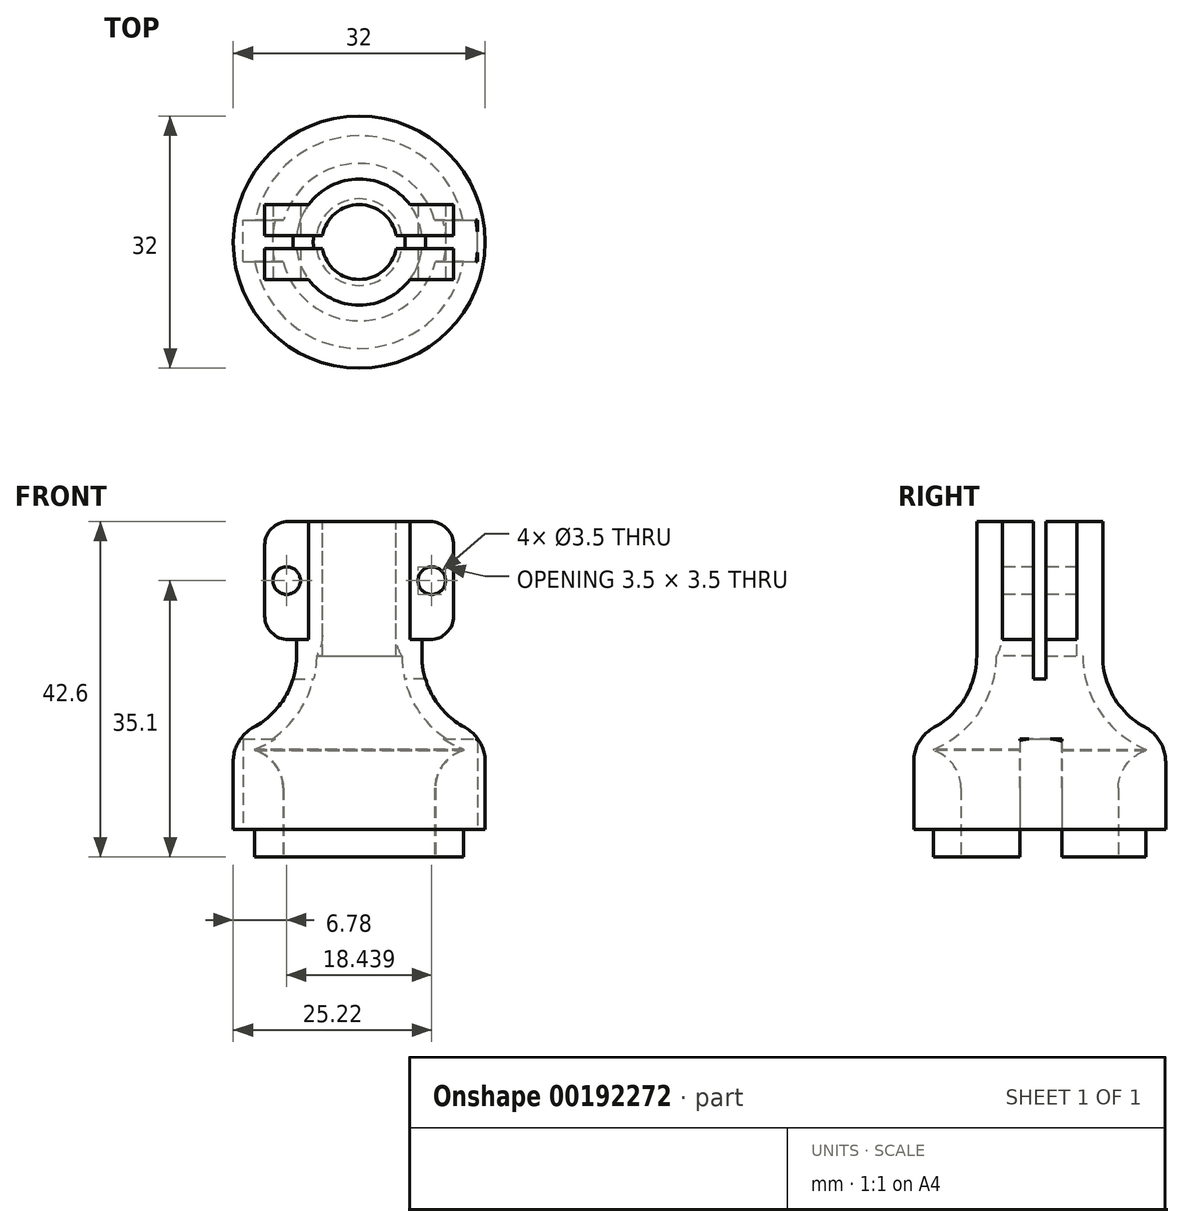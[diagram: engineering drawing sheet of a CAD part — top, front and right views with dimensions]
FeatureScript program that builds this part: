
annotation { "Feature Type Name" : "Feature", "Feature Type Description" : "" }
export const myFeature = defineFeature(function(context is Context, id is Id, definition is map)
    precondition{}
    {
        {
            var Q0;
            Q0=qCreatedBy(makeId("Front.planeOp"),FACE);
            var sketch = newSketch(context, id + "F0", { "sketchPlane" : qUnion([Q0])});
            skLineSegment(sketch, "E0", {"start": v(0, 0) * mm, "end": v(16, 0) * mm});
            skLineSegment(sketch, "E1", {"start": v(16, 0) * mm, "end": v(16, 12) * mm});
            skPoint(sketch, "E2.endSnap0", {"position": v(8, 12) * mm});
            skLineSegment(sketch, "E3", {"start": v(8, 22) * mm, "end": v(8, 34.1) * mm});
            skLineSegment(sketch, "E4", {"start": v(8, 34.1) * mm, "end": v(0, 34.1) * mm});
            skArc(sketch, "E5", {"start": v(8, 22) * mm, "mid": v(10.25, 15.6) * mm, "end": v(16, 12) * mm});
            skLineSegment(sketch, "E6.1", {"start": v(0, 2.5) * mm, "end": v(13.5, 2.5) * mm});
            skLineSegment(sketch, "E6.2", {"start": v(13.5, 2.5) * mm, "end": v(13.5, 10.17) * mm});
            skArc(sketch, "E6.3", {"start": v(5.5, 22) * mm, "mid": v(7.69, 14.86) * mm, "end": v(13.5, 10.17) * mm});
            skLineSegment(sketch, "E7", {"start": v(0, 31.6) * mm, "end": v(0, 34.1) * mm});
            skLineSegment(sketch, "E8", {"start": v(0, 0) * mm, "end": v(0, 2.5) * mm});
            skLineSegment(sketch, "E9", {"start": v(0, 31.6) * mm, "end": v(0, 22) * mm});
            skLineSegment(sketch, "E10", {"start": v(0, 22) * mm, "end": v(5.5, 22) * mm});
            skSolve(sketch);
        }
        {
            var Q0;
            Q0 = qSketchRegion(id + "F0", true);
            var Q1;
            Q1=sQuery(id+"F0.wireOp",EDGE,"E8");
            revolve(context, id + "F1", {"entities" : qUnion([Q0]), "axis" : qUnion([Q1]), "revolveType" : RevolveType.FULL});
        }
        {
            var Q0;
            Q0=makeQuery(id+"F1.opRevolve","SWEPT_EDGE",EDGE,{"disambiguationData":[OSD([sQuery(id+"F0.wireOp",EDGE,"E1"),sQuery(id+"F0.wireOp",EDGE,"E5")])]});
            fillet(context, id + "F2", {"entities" : qUnion([Q0]), "radius" : 5 * mm, "tangentPropagation" : true, "allowEdgeOverflow" : false});
        }
        {
            var Q0;
            Q0=makeQuery(id+"F1.opRevolve","SWEPT_FACE",FACE,{"disambiguationData":[OSD([sQuery(id+"F0.wireOp",EDGE,"E0")])]});
            var sketch = newSketch(context, id + "F3", { "sketchPlane" : qUnion([Q0])});
            skCircle(sketch, "E11", {"center": v(0, 0) * mm, "radius": 13.5 * mm});
            skSolve(sketch);
        }
        {
            var Q0;
            Q0=makeQuery(id+"F3.imprint","IMPRINT",FACE,{"disambiguationData":[TD([[makeQuery(id+"F3.imprint","IMPRINT",EDGE,{"derivedFrom":sQuery(id+"F3.wireOp",EDGE,"E11")}),1.0]])]});
            extrude(context, id + "F4", {"entities" : qUnion([Q0]), "operationType" : NewBodyOperationType.REMOVE, "oppositeDirection" : true, "depth" : 8 * mm});
        }
        {
            var Q0;
            Q0=makeQuery(id+"F1.opRevolve","SWEPT_FACE",FACE,{"disambiguationData":[OSD([sQuery(id+"F0.wireOp",EDGE,"E4")])]});
            var sketch = newSketch(context, id + "F5", { "sketchPlane" : qUnion([Q0])});
            skCircle(sketch, "E12", {"center": v(0, 0) * mm, "radius": 4.75 * mm});
            skSolve(sketch);
        }
        {
            var Q0;
            Q0 = qSketchRegion(id + "F5", true);
            extrude(context, id + "F6", {"entities" : qUnion([Q0]), "operationType" : NewBodyOperationType.REMOVE, "oppositeDirection" : true, "depth" : 25 * mm});
        }
        {
            var Q0;
            Q0=makeQuery(id+"F1.opRevolve","SWEPT_FACE",FACE,{"disambiguationData":[OSD([sQuery(id+"F0.wireOp",EDGE,"E4")])]});
            var sketch = newSketch(context, id + "F7", { "sketchPlane" : qUnion([Q0])});
            skCircle(sketch, "E13", {"center": v(0, 0) * mm, "radius": 8 * mm});
            skLineSegment(sketch, "E14", {"start": v(0, 0) * mm, "end": v(0, 4.75) * mm});
            skLineSegment(sketch, "E15", {"start": v(0, 4.75) * mm, "end": v(12, 4.75) * mm});
            skLineSegment(sketch, "E16", {"start": v(0, -4.75) * mm, "end": v(12, -4.75) * mm});
            skLineSegment(sketch, "E17", {"start": v(12, -4.75) * mm, "end": v(12, 4.75) * mm});
            skLineSegment(sketch, "E18", {"start": v(0, 4.75) * mm, "end": v(-12, 4.75) * mm});
            skLineSegment(sketch, "E19", {"start": v(0, -4.75) * mm, "end": v(-12, -4.75) * mm});
            skLineSegment(sketch, "E20", {"start": v(-12, -4.75) * mm, "end": v(-12, 4.75) * mm});
            skCircle(sketch, "E21", {"center": v(0, 0) * mm, "radius": 4.75 * mm});
            skSolve(sketch);
        }
        {
            var Q0;
            Q0 = qSketchRegion(id + "F7", true);
            extrude(context, id + "F8", {"entities" : qUnion([Q0]), "operationType" : NewBodyOperationType.ADD, "oppositeDirection" : true, "depth" : 10 * mm});
        }
        {
            var Q0;
            Q0 = qSketchRegion(id + "F7", true);
            extrude(context, id + "F9", {"entities" : qUnion([Q0]), "operationType" : NewBodyOperationType.ADD, "depth" : 5 * mm});
        }
        {
            var Q0;
            {var subQ0=sQuery(id+"F7.wireOp",EDGE,"E19");Q0=makeQuery(id+"F9.boolean.opBoolean","MERGE",FACE,{"derivedFrom":[makeQuery(id+"F8.opExtrude","SWEPT_FACE",FACE,{"disambiguationData":[OSD([subQ0])]}),makeQuery(id+"F9.opExtrude","SWEPT_FACE",FACE,{"disambiguationData":[OSD([subQ0])]})]});}
            var sketch = newSketch(context, id + "F10", { "sketchPlane" : qUnion([Q0])});
            skLineSegment(sketch, "E22", {"start": v(-12, 31.6) * mm, "end": v(-9.22, 31.6) * mm});
            skPoint(sketch, "E22.endSnap0", {"position": v(-9.22, 39.1) * mm});
            skCircle(sketch, "E23", {"center": v(-9.22, 31.6) * mm, "radius": 1.75 * mm});
            skSolve(sketch);
        }
        {
            var Q0;
            Q0 = qSketchRegion(id + "F10", true);
            extrude(context, id + "F11", {"entities" : qUnion([Q0]), "operationType" : NewBodyOperationType.REMOVE, "oppositeDirection" : true, "depth" : 15 * mm});
        }
        {
            var Q0;
            {var subQ0=sQuery(id+"F7.wireOp",EDGE,"E16");Q0=makeQuery(id+"F9.boolean.opBoolean","MERGE",FACE,{"derivedFrom":[makeQuery(id+"F8.opExtrude","SWEPT_FACE",FACE,{"disambiguationData":[OSD([subQ0])]}),makeQuery(id+"F9.opExtrude","SWEPT_FACE",FACE,{"disambiguationData":[OSD([subQ0])]})]});}
            var sketch = newSketch(context, id + "F12", { "sketchPlane" : qUnion([Q0])});
            skLineSegment(sketch, "E24", {"start": v(12, 31.6) * mm, "end": v(9.22, 31.6) * mm});
            skPoint(sketch, "E24.endSnap0", {"position": v(9.22, 39.1) * mm});
            skCircle(sketch, "E25", {"center": v(9.22, 31.6) * mm, "radius": 1.75 * mm});
            skSolve(sketch);
        }
        {
            var Q0;
            Q0 = qSketchRegion(id + "F12", true);
            extrude(context, id + "F13", {"entities" : qUnion([Q0]), "operationType" : NewBodyOperationType.REMOVE, "oppositeDirection" : true, "depth" : 15 * mm});
        }
        {
            var Q0;
            Q0=makeQuery(id+"F9.opExtrude","CAP_FACE",FACE,{"disambiguationData":[OSD([sQuery(id+"F7.wireOp",EDGE,"E13"),sQuery(id+"F7.wireOp",EDGE,"E15"),sQuery(id+"F7.wireOp",EDGE,"E16"),sQuery(id+"F7.wireOp",EDGE,"E17"),sQuery(id+"F7.wireOp",EDGE,"E18"),sQuery(id+"F7.wireOp",EDGE,"E19"),sQuery(id+"F7.wireOp",EDGE,"E20"),sQuery(id+"F7.wireOp",EDGE,"E21")])],"isStart":false});
            var sketch = newSketch(context, id + "F14", { "sketchPlane" : qUnion([Q0])});
            skLineSegment(sketch, "E26", {"start": v(-12, 0) * mm, "end": v(-12, 0.8) * mm});
            skLineSegment(sketch, "E27", {"start": v(-12, 0.8) * mm, "end": v(-4.68, 0.8) * mm});
            skLineSegment(sketch, "E28", {"start": v(-12, 0) * mm, "end": v(-12, -0.8) * mm});
            skLineSegment(sketch, "E29", {"start": v(-12, -0.8) * mm, "end": v(-4.68, -0.8) * mm});
            skLineSegment(sketch, "E30", {"start": v(12, 0) * mm, "end": v(12, 0.8) * mm});
            skLineSegment(sketch, "E31", {"start": v(12, 0.8) * mm, "end": v(4.68, 0.8) * mm});
            skLineSegment(sketch, "E32", {"start": v(12, 0) * mm, "end": v(12, -0.8) * mm});
            skLineSegment(sketch, "E33", {"start": v(12, -0.8) * mm, "end": v(4.68, -0.8) * mm});
            skSolve(sketch);
        }
        {
            var Q0;
            Q0 = qSketchRegion(id + "F14", true);
            var Q1;
            Q1=makeQuery(id+"F14.imprint","IMPRINT",FACE,{"disambiguationData":[TD([[makeQuery(id+"F14.imprint","IMPRINT",EDGE,{"derivedFrom":sQuery(id+"F14.wireOp",EDGE,"E26")}),-1.0]])]});
            var Q2;
            Q2=makeQuery(id+"F14.imprint","IMPRINT",FACE,{"disambiguationData":[TD([[makeQuery(id+"F14.imprint","IMPRINT",EDGE,{"derivedFrom":sQuery(id+"F14.wireOp",EDGE,"E30")}),1.0]])]});
            extrude(context, id + "F15", {"entities" : qUnion([Q0, Q1, Q2]), "operationType" : NewBodyOperationType.REMOVE, "oppositeDirection" : true, "depth" : 20 * mm});
        }
        {
            var Q0;
            {var subQ0=sQuery(id+"F7.wireOp",EDGE,"E19");var subQ1=sQuery(id+"F7.wireOp",EDGE,"E20");Q0=makeQuery(id+"F15.boolean.opBoolean","SPLIT",EDGE,{"disambiguationData":[TD([makeQuery(id+"F8.opExtrude","SWEPT_FACE",FACE,{"disambiguationData":[OSD([subQ0])]})])],"derivedFrom":makeQuery(id+"F9.opExtrude","CAP_EDGE",EDGE,{"disambiguationData":[OSD([subQ1])],"isStart":false})});}
            var Q1;
            {var subQ0=sQuery(id+"F7.wireOp",EDGE,"E17");var subQ1=sQuery(id+"F7.wireOp",EDGE,"E16");Q1=makeQuery(id+"F15.boolean.opBoolean","SPLIT",EDGE,{"disambiguationData":[TD([makeQuery(id+"F8.opExtrude","SWEPT_FACE",FACE,{"disambiguationData":[OSD([subQ1])]})])],"derivedFrom":makeQuery(id+"F9.opExtrude","CAP_EDGE",EDGE,{"disambiguationData":[OSD([subQ0])],"isStart":false})});}
            var Q2;
            {var subQ0=sQuery(id+"F7.wireOp",EDGE,"E18");var subQ1=sQuery(id+"F7.wireOp",EDGE,"E20");Q2=makeQuery(id+"F15.boolean.opBoolean","SPLIT",EDGE,{"disambiguationData":[TD([makeQuery(id+"F8.opExtrude","SWEPT_FACE",FACE,{"disambiguationData":[OSD([subQ0])]})])],"derivedFrom":makeQuery(id+"F9.opExtrude","CAP_EDGE",EDGE,{"disambiguationData":[OSD([subQ1])],"isStart":false})});}
            var Q3;
            {var subQ0=sQuery(id+"F7.wireOp",EDGE,"E15");var subQ1=sQuery(id+"F7.wireOp",EDGE,"E17");Q3=makeQuery(id+"F15.boolean.opBoolean","SPLIT",EDGE,{"disambiguationData":[TD([makeQuery(id+"F8.opExtrude","SWEPT_FACE",FACE,{"disambiguationData":[OSD([subQ0])]})])],"derivedFrom":makeQuery(id+"F9.opExtrude","CAP_EDGE",EDGE,{"disambiguationData":[OSD([subQ1])],"isStart":false})});}
            var Q4;
            {var subQ0=sQuery(id+"F7.wireOp",EDGE,"E19");var subQ1=sQuery(id+"F7.wireOp",EDGE,"E20");Q4=makeQuery(id+"F15.boolean.opBoolean","SPLIT",EDGE,{"disambiguationData":[TD([makeQuery(id+"F8.opExtrude","SWEPT_FACE",FACE,{"disambiguationData":[OSD([subQ0])]})])],"derivedFrom":makeQuery(id+"F8.opExtrude","CAP_EDGE",EDGE,{"disambiguationData":[OSD([subQ1])],"isStart":false})});}
            var Q5;
            {var subQ0=sQuery(id+"F7.wireOp",EDGE,"E18");var subQ1=sQuery(id+"F7.wireOp",EDGE,"E20");Q5=makeQuery(id+"F15.boolean.opBoolean","SPLIT",EDGE,{"disambiguationData":[TD([makeQuery(id+"F8.opExtrude","SWEPT_FACE",FACE,{"disambiguationData":[OSD([subQ0])]})])],"derivedFrom":makeQuery(id+"F8.opExtrude","CAP_EDGE",EDGE,{"disambiguationData":[OSD([subQ1])],"isStart":false})});}
            var Q6;
            {var subQ0=sQuery(id+"F7.wireOp",EDGE,"E16");var subQ1=sQuery(id+"F7.wireOp",EDGE,"E17");Q6=makeQuery(id+"F15.boolean.opBoolean","SPLIT",EDGE,{"disambiguationData":[TD([makeQuery(id+"F8.opExtrude","SWEPT_FACE",FACE,{"disambiguationData":[OSD([subQ0])]})])],"derivedFrom":makeQuery(id+"F8.opExtrude","CAP_EDGE",EDGE,{"disambiguationData":[OSD([subQ1])],"isStart":false})});}
            var Q7;
            {var subQ0=sQuery(id+"F7.wireOp",EDGE,"E15");var subQ1=sQuery(id+"F7.wireOp",EDGE,"E17");Q7=makeQuery(id+"F15.boolean.opBoolean","SPLIT",EDGE,{"disambiguationData":[TD([makeQuery(id+"F8.opExtrude","SWEPT_FACE",FACE,{"disambiguationData":[OSD([subQ0])]})])],"derivedFrom":makeQuery(id+"F8.opExtrude","CAP_EDGE",EDGE,{"disambiguationData":[OSD([subQ1])],"isStart":false})});}
            fillet(context, id + "F16", {"entities" : qUnion([Q0, Q1, Q2, Q3, Q4, Q5, Q6, Q7]), "radius" : 3 * mm, "tangentPropagation" : true, "allowEdgeOverflow" : false});
        }
        {
            var Q0;
            Q0=makeQuery(id+"F1.opRevolve","SWEPT_FACE",FACE,{"disambiguationData":[OSD([sQuery(id+"F0.wireOp",EDGE,"E0")])]});
            var sketch = newSketch(context, id + "F17", { "sketchPlane" : qUnion([Q0])});
            skCircle(sketch, "E34", {"center": v(0, 0) * mm, "radius": 13.5 * mm});
            skCircle(sketch, "E35", {"center": v(0, 0) * mm, "radius": 10 * mm});
            skSolve(sketch);
        }
        {
            var Q0;
            Q0=makeQuery(id+"F17.imprint","IMPRINT",FACE,{"disambiguationData":[TD([[makeQuery(id+"F17.imprint","IMPRINT",EDGE,{"derivedFrom":sQuery(id+"F17.wireOp",EDGE,"E34")}),1.0]])]});
            extrude(context, id + "F18", {"entities" : qUnion([Q0]), "oppositeDirection" : true, "depth" : 10 * mm});
        }
        {
            var Q0;
            Q0=makeQuery(id+"F18.opExtrude","CAP_FACE",FACE,{"disambiguationData":[OSD([sQuery(id+"F17.wireOp",EDGE,"E34"),sQuery(id+"F17.wireOp",EDGE,"E35")])],"isStart":true});
            extrude(context, id + "F19", {"entities" : qUnion([Q0]), "operationType" : NewBodyOperationType.ADD, "depth" : 3.5 * mm});
        }
        {
            var Q0;
            Q0=makeQuery(id+"F18.opExtrude","CAP_EDGE",EDGE,{"disambiguationData":[OSD([sQuery(id+"F17.wireOp",EDGE,"E35")])],"isStart":false});
            fillet(context, id + "F20", {"entities" : qUnion([Q0]), "radius" : 5 * mm, "tangentPropagation" : true, "allowEdgeOverflow" : false});
        }
        {
            var Q0;
            {var subQ0=makeQuery(id+"F6.opExtrude","SWEPT_FACE",FACE,{"disambiguationData":[OSD([sQuery(id+"F5.wireOp",EDGE,"E12")])]});var subQ1=makeQuery(id+"F1.opRevolve","SWEPT_FACE",FACE,{"disambiguationData":[OSD([sQuery(id+"F0.wireOp",EDGE,"E10")])]});Q0=makeQuery(id+"F15.boolean.opBoolean","SPLIT",EDGE,{"disambiguationData":[TD([makeQuery(id+"F15.opExtrude","SWEPT_FACE",FACE,{"disambiguationData":[OSD([sQuery(id+"F14.wireOp",EDGE,"E29")])]})])],"derivedFrom":makeQuery(id+"F6.boolean.opBoolean","INTERSECT",EDGE,{"derivedFrom":[subQ1,subQ0]})});}
            fillet(context, id + "F21", {"entities" : qUnion([Q0]), "radius" : 5 * mm, "tangentPropagation" : true, "allowEdgeOverflow" : false});
        }
        {
            var Q0;
            Q0=makeQuery(id+"F19.opExtrude","CAP_FACE",FACE,{"disambiguationData":[OSD([sQuery(id+"F17.wireOp",EDGE,"E34"),sQuery(id+"F17.wireOp",EDGE,"E35")])],"isStart":false});
            var sketch = newSketch(context, id + "F22", { "sketchPlane" : qUnion([Q0])});
            skLineSegment(sketch, "E36.top", {"start": v(0, 2.5) * mm, "end": v(15, 2.5) * mm});
            skLineSegment(sketch, "E36.right", {"start": v(15, 0) * mm, "end": v(15, 2.5) * mm});
            skLineSegment(sketch, "E37.top", {"start": v(0, -2.82) * mm, "end": v(15, -2.82) * mm});
            skLineSegment(sketch, "E37.right", {"start": v(15, 0) * mm, "end": v(15, -2.82) * mm});
            skLineSegment(sketch, "E38.bottom", {"start": v(0, 2.5) * mm, "end": v(-14.75, 2.5) * mm});
            skLineSegment(sketch, "E38.top", {"start": v(0, -2.82) * mm, "end": v(-14.75, -2.82) * mm});
            skLineSegment(sketch, "E38.left", {"start": v(0, 2.5) * mm, "end": v(0, -2.82) * mm});
            skLineSegment(sketch, "E38.right", {"start": v(-14.75, 2.5) * mm, "end": v(-14.75, -2.82) * mm});
            skSolve(sketch);
        }
        {
            var Q0;
            Q0 = qSketchRegion(id + "F22", true);
            extrude(context, id + "F23", {"entities" : qUnion([Q0]), "operationType" : NewBodyOperationType.REMOVE, "oppositeDirection" : true, "depth" : 15 * mm});
        }
    });
